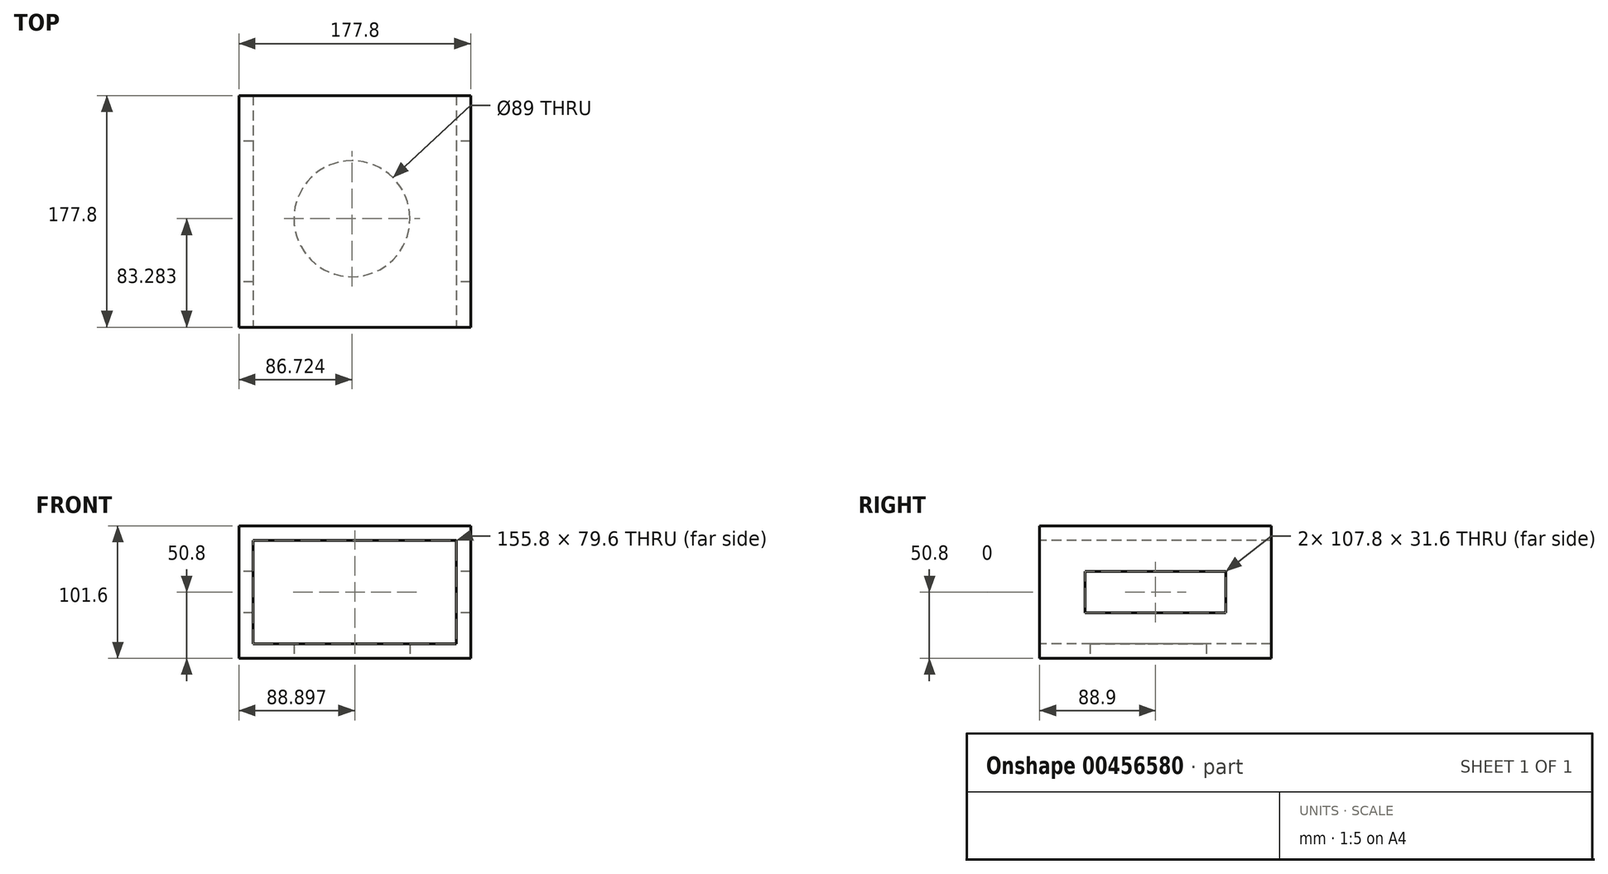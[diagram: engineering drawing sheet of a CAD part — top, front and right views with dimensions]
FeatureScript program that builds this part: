
annotation { "Feature Type Name" : "Feature", "Feature Type Description" : "" }
export const myFeature = defineFeature(function(context is Context, id is Id, definition is map)
    precondition{}
    {
        {
            var Q0;
            Q0=qCreatedBy(makeId("Top.planeOp"),FACE);
            var sketch = newSketch(context, id + "F0", { "sketchPlane" : qUnion([Q0])});
            skLineSegment(sketch, "E0.bottom", {"start": v(-96.01, 90.17) * mm, "end": v(81.79, 90.17) * mm});
            skLineSegment(sketch, "E0.top", {"start": v(-96.01, -87.63) * mm, "end": v(81.79, -87.63) * mm});
            skLineSegment(sketch, "E0.left", {"start": v(-96.01, 90.17) * mm, "end": v(-96.01, -87.63) * mm});
            skLineSegment(sketch, "E0.right", {"start": v(81.79, 90.17) * mm, "end": v(81.79, -87.63) * mm});
            skSolve(sketch);
        }
        {
            var Q0;
            Q0=makeQuery(id+"F0.imprint","IMPRINT",FACE,{"disambiguationData":[TD([[makeQuery(id+"F0.imprint","IMPRINT",EDGE,{"derivedFrom":sQuery(id+"F0.wireOp",EDGE,"E0.bottom")}),-1.0]])]});
            extrude(context, id + "F1", {"entities" : qUnion([Q0]), "oppositeDirection" : true, "depth" : 101.6 * mm});
        }
        {
            var Q0;
            Q0=makeQuery(id+"F1.opExtrude","SWEPT_FACE",FACE,{"disambiguationData":[OSD([sQuery(id+"F0.wireOp",EDGE,"E0.top")])]});
            var sketch = newSketch(context, id + "F2", { "sketchPlane" : qUnion([Q0])});
            skLineSegment(sketch, "E1.bottom", {"start": v(-85.01, -11) * mm, "end": v(70.79, -11) * mm});
            skLineSegment(sketch, "E1.top", {"start": v(-85.01, -90.6) * mm, "end": v(70.79, -90.6) * mm});
            skLineSegment(sketch, "E1.left", {"start": v(-85.01, -11) * mm, "end": v(-85.01, -90.6) * mm});
            skLineSegment(sketch, "E1.right", {"start": v(70.79, -11) * mm, "end": v(70.79, -90.6) * mm});
            skLineSegment(sketch, "E2.0", {"start": v(-96.01, 0) * mm, "end": v(81.79, 0) * mm});
            skLineSegment(sketch, "E2.1", {"start": v(-96.01, -101.6) * mm, "end": v(-96.01, 0) * mm});
            skLineSegment(sketch, "E2.2", {"start": v(-96.01, -101.6) * mm, "end": v(81.79, -101.6) * mm});
            skLineSegment(sketch, "E2.3", {"start": v(81.79, -101.6) * mm, "end": v(81.79, 0) * mm});
            skSolve(sketch);
        }
        {
            var Q0;
            Q0=makeQuery(id+"F2.imprint","IMPRINT",FACE,{"disambiguationData":[TD([[makeQuery(id+"F2.imprint","IMPRINT",EDGE,{"derivedFrom":sQuery(id+"F2.wireOp",EDGE,"E1.bottom")}),-1.0]])]});
            extrude(context, id + "F3", {"entities" : qUnion([Q0]), "operationType" : NewBodyOperationType.REMOVE, "endBound" : BoundingType.THROUGH_ALL, "oppositeDirection" : true, "depth" : 25 * mm});
        }
        {
            var Q0;
            Q0=makeQuery(id+"F1.opExtrude","SWEPT_FACE",FACE,{"disambiguationData":[OSD([sQuery(id+"F0.wireOp",EDGE,"E0.left")])]});
            var sketch = newSketch(context, id + "F4", { "sketchPlane" : qUnion([Q0])});
            skLineSegment(sketch, "E3.bottom", {"start": v(-55.17, -35) * mm, "end": v(52.63, -35) * mm});
            skLineSegment(sketch, "E3.top", {"start": v(-55.17, -66.6) * mm, "end": v(52.63, -66.6) * mm});
            skLineSegment(sketch, "E3.left", {"start": v(-55.17, -35) * mm, "end": v(-55.17, -66.6) * mm});
            skLineSegment(sketch, "E3.right", {"start": v(52.63, -35) * mm, "end": v(52.63, -66.6) * mm});
            skSolve(sketch);
        }
        {
            var Q0;
            Q0=makeQuery(id+"F4.imprint","IMPRINT",FACE,{"disambiguationData":[TD([[makeQuery(id+"F4.imprint","IMPRINT",EDGE,{"derivedFrom":sQuery(id+"F4.wireOp",EDGE,"E3.bottom")}),-1.0]])]});
            extrude(context, id + "F5", {"entities" : qUnion([Q0]), "operationType" : NewBodyOperationType.REMOVE, "endBound" : BoundingType.THROUGH_ALL, "oppositeDirection" : true, "depth" : 25 * mm});
        }
        {
            var Q0;
            Q0=makeQuery(id+"F1.opExtrude","CAP_FACE",FACE,{"disambiguationData":[OSD([sQuery(id+"F0.wireOp",EDGE,"E0.bottom"),sQuery(id+"F0.wireOp",EDGE,"E0.top"),sQuery(id+"F0.wireOp",EDGE,"E0.left"),sQuery(id+"F0.wireOp",EDGE,"E0.right")])],"isStart":false});
            var sketch = newSketch(context, id + "F6", { "sketchPlane" : qUnion([Q0])});
            skCircle(sketch, "E4", {"center": v(-9.29, 4.35) * mm, "radius": 44.5 * mm});
            skSolve(sketch);
        }
        {
            var Q0;
            Q0 = qSketchRegion(id + "F6", true);
            extrude(context, id + "F7", {"entities" : qUnion([Q0]), "operationType" : NewBodyOperationType.REMOVE, "oppositeDirection" : true, "depth" : 25 * mm});
        }
    });
